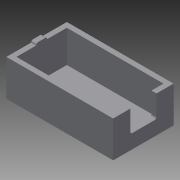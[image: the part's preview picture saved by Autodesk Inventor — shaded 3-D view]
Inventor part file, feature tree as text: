
AUTODESK INVENTOR PART (.ipt)
format: ipt  version: 2015 (Build 190159000, 159)  size: 129,024 bytes
history: native  units: mm
features: extrude x4, sketch x4, hole x1, fillet x1
ambient origin geometry x8: Origin, YZ Plane, XZ Plane, XY Plane, X Axis, Y Axis, Z Axis, Center Point
bodies: Volumenkörper1 (feature_tree)
feature tree (10):
  extrude  "Extrusion1"  Depth=53.0mm
  extrude  "Extrusion2"  Depth=25.0mm
  extrude  "Extrusion8"  Depth=2.5mm
  hole  "Bohrung2"  [1 undecoded]
  extrude  "Extrusion9"  Depth=2.5mm
  fillet  "Rundung2"  Radius=16.0mm
  sketch  "Skizze1"  dims[d0=30.0mm d1=53.0mm]
  sketch  "Skizze2"  dims[d2=2.0mm d3=0.0mm d4=25.0mm]
  sketch  "Skizze8"  dims[d5=48.0mm d6=2.5mm]
  sketch  "Skizze9"  dims[d7=2.5mm d8=2.5mm d9=2.5mm d10=16.0mm d11=0.0mm d49=13.0mm d50=8.5mm d51=8.5mm d52=11.0mm d53=0.0mm d54=12.5mm d55=15.0mm d56=3.0mm d57=6.0mm d58=4.0mm d59=2.0mm d60=90.0deg d61=8.0mm d62=20.594885mm d63=5.5mm d64=12.25mm d65=12.25mm d66=1.0mm d67=0.0mm d68=1.0mm]
note: 1 required parameter value undecoded (feature->parameter linkage not recoverable at this tier; creation-order binding heuristic only, values carry confidence <= 0.55)
